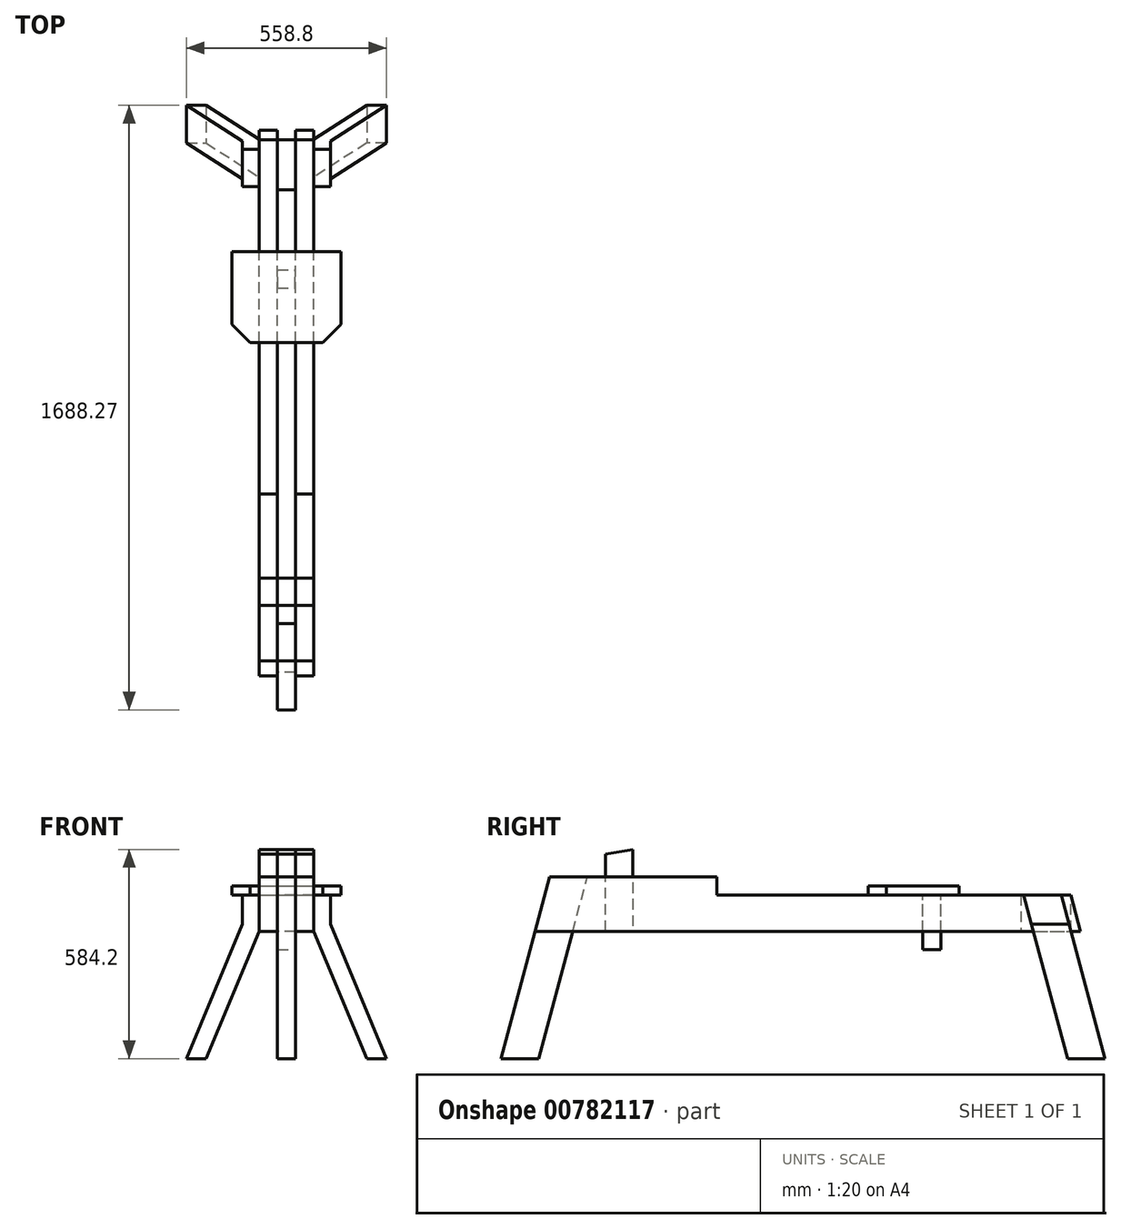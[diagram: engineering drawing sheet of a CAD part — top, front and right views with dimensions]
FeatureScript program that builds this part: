
annotation { "Feature Type Name" : "Feature", "Feature Type Description" : "" }
export const myFeature = defineFeature(function(context is Context, id is Id, definition is map)
    precondition{}
    {
        {
            var Q0;
            Q0=qCreatedBy(makeId("Right.planeOp"),FACE);
            cPlane(context, id + "F0", {"entities" : qUnion([Q0]), "cplaneType" : CPlaneType.OFFSET, "offset" : 25.4 * mm, "width" : 152.4 * mm, "height" : 152.4 * mm});
        }
        {
            var Q0;
            Q0=qCreatedBy(id+"F0.planeOp",FACE);
            var sketch = newSketch(context, id + "F1", { "sketchPlane" : qUnion([Q0])});
            skLineSegment(sketch, "E0", {"start": v(0, 0) * mm, "end": v(-40.84, -152.4) * mm});
            skLineSegment(sketch, "E1", {"start": v(0, 0) * mm, "end": v(467.16, 0) * mm});
            skLineSegment(sketch, "E2.0", {"start": v(-40.84, -152.4) * mm, "end": v(1483.16, -152.4) * mm});
            skLineSegment(sketch, "E3", {"start": v(467.16, 0) * mm, "end": v(467.16, -50.8) * mm});
            skLineSegment(sketch, "E4", {"start": v(467.16, -50.8) * mm, "end": v(1455.94, -50.8) * mm});
            skLineSegment(sketch, "E5", {"start": v(1455.94, -50.8) * mm, "end": v(1483.16, -152.4) * mm});
            skSolve(sketch);
        }
        {
            var Q0;
            Q0 = qSketchRegion(id + "F1", true);
            extrude(context, id + "F2", {"entities" : qUnion([Q0]), "depth" : 50.8 * mm, "offsetDistance" : 25.4 * mm});
        }
        {
            var Q0;
            Q0=qCreatedBy(makeId("Right.planeOp"),FACE);
            var sketch = newSketch(context, id + "F3", { "sketchPlane" : qUnion([Q0])});
            skLineSegment(sketch, "E6", {"start": v(0, 0) * mm, "end": v(-136.12, -508) * mm});
            skLineSegment(sketch, "E7", {"start": v(-136.12, -508) * mm, "end": v(-30.93, -508) * mm});
            skLineSegment(sketch, "E8", {"start": v(-30.93, -508) * mm, "end": v(105.18, 0) * mm});
            skLineSegment(sketch, "E9", {"start": v(105.18, 0) * mm, "end": v(0, 0) * mm});
            skSolve(sketch);
        }
        {
            var Q0;
            Q0 = qSketchRegion(id + "F3", true);
            extrude(context, id + "F4", {"entities" : qUnion([Q0]), "depth" : 50.8 * mm, "offsetDistance" : 25.4 * mm, "symmetric" : true});
        }
        {
            var Q0;
            Q0=makeQuery(id+"F2.opExtrude","CAP_FACE",FACE,{"disambiguationData":[OSD([sQuery(id+"F1.wireOp",EDGE,"E0"),sQuery(id+"F1.wireOp",EDGE,"E1"),sQuery(id+"F1.wireOp",EDGE,"E2.0"),sQuery(id+"F1.wireOp",EDGE,"E3"),sQuery(id+"F1.wireOp",EDGE,"E4"),sQuery(id+"F1.wireOp",EDGE,"E5")])],"isStart":false});
            var sketch = newSketch(context, id + "F5", { "sketchPlane" : qUnion([Q0])});
            skLineSegment(sketch, "E10", {"start": v(1324.46, -50.8) * mm, "end": v(1446.97, -508) * mm});
            skLineSegment(sketch, "E11", {"start": v(1446.97, -508) * mm, "end": v(1552.15, -508) * mm});
            skLineSegment(sketch, "E12", {"start": v(1552.15, -508) * mm, "end": v(1429.64, -50.8) * mm});
            skLineSegment(sketch, "E13", {"start": v(1429.64, -50.8) * mm, "end": v(1324.46, -50.8) * mm});
            skSolve(sketch);
        }
        {
            var Q0;
            Q0 = qSketchRegion(id + "F5", true);
            extrude(context, id + "F6", {"entities" : qUnion([Q0]), "depth" : 203.2 * mm, "offsetDistance" : 25.4 * mm});
        }
        {
            var Q0;
            Q0=qCreatedBy(makeId("Front.planeOp"),FACE);
            var sketch = newSketch(context, id + "F7", { "sketchPlane" : qUnion([Q0])});
            skLineSegment(sketch, "E14", {"start": v(76.2, -152.4) * mm, "end": v(224.37, -508) * mm});
            skLineSegment(sketch, "E15", {"start": v(224.37, -508) * mm, "end": v(279.4, -508) * mm, "construction": true});
            skLineSegment(sketch, "E16", {"start": v(279.4, -508) * mm, "end": v(123.1, -132.86) * mm});
            skLineSegment(sketch, "E17", {"start": v(123.1, -132.86) * mm, "end": v(123.1, -50.8) * mm});
            skLineSegment(sketch, "E18", {"start": v(123.1, -50.8) * mm, "end": v(76.2, -50.8) * mm, "construction": true});
            skLineSegment(sketch, "E19", {"start": v(76.2, -50.8) * mm, "end": v(76.2, -152.4) * mm});
            skLineSegment(sketch, "E20", {"start": v(76.2, -152.4) * mm, "end": v(123.1, -132.86) * mm, "construction": true});
            skLineSegment(sketch, "E21", {"start": v(123.1, -50.8) * mm, "end": v(279.4, -50.8) * mm});
            skLineSegment(sketch, "E22", {"start": v(279.4, -50.8) * mm, "end": v(279.4, -508) * mm});
            skLineSegment(sketch, "E23", {"start": v(224.37, -508) * mm, "end": v(76.2, -508) * mm});
            skLineSegment(sketch, "E24", {"start": v(76.2, -508) * mm, "end": v(76.2, -152.4) * mm});
            skSolve(sketch);
        }
        {
            var Q0;
            Q0 = qSketchRegion(id + "F7", true);
            extrude(context, id + "F8", {"entities" : qUnion([Q0]), "operationType" : NewBodyOperationType.REMOVE, "endBound" : BoundingType.THROUGH_ALL, "oppositeDirection" : true, "depth" : 25.4 * mm, "offsetDistance" : 25.4 * mm});
        }
        {
            var Q0;
            Q0=makeQuery(id+"F2.opExtrude","SWEPT_BODY",BODY,{"disambiguationData":[OSD([sQuery(id+"F1.wireOp",EDGE,"E0"),sQuery(id+"F1.wireOp",EDGE,"E1"),sQuery(id+"F1.wireOp",EDGE,"E2.0"),sQuery(id+"F1.wireOp",EDGE,"E3"),sQuery(id+"F1.wireOp",EDGE,"E4"),sQuery(id+"F1.wireOp",EDGE,"E5")])]});
            var Q1;
            Q1=makeQuery(id+"F6.opExtrude","SWEPT_BODY",BODY,{"disambiguationData":[OSD([sQuery(id+"F5.wireOp",EDGE,"E10"),sQuery(id+"F5.wireOp",EDGE,"E11"),sQuery(id+"F5.wireOp",EDGE,"E12"),sQuery(id+"F5.wireOp",EDGE,"E13")])]});
            var Q2;
            Q2=qCreatedBy(makeId("Right.planeOp"),FACE);
            mirror(context, id + "F9", {"entities" : qUnion([Q0, Q1]), "mirrorPlane" : qUnion([Q2])});
        }
        {
            var Q0;
            Q0=qCreatedBy(makeId("Right.planeOp"),FACE);
            var sketch = newSketch(context, id + "F10", { "sketchPlane" : qUnion([Q0])});
            skLineSegment(sketch, "E25", {"start": v(1455.94, -152.4) * mm, "end": v(1455.94, -50.8) * mm});
            skLineSegment(sketch, "E26", {"start": v(1455.94, -50.8) * mm, "end": v(1316.24, -50.8) * mm});
            skLineSegment(sketch, "E27", {"start": v(1316.24, -50.8) * mm, "end": v(1316.24, -152.4) * mm});
            skLineSegment(sketch, "E28", {"start": v(1316.24, -152.4) * mm, "end": v(1455.94, -152.4) * mm});
            skSolve(sketch);
        }
        {
            var Q0;
            Q0 = qSketchRegion(id + "F10", true);
            extrude(context, id + "F11", {"entities" : qUnion([Q0]), "depth" : 50.8 * mm, "offsetDistance" : 25.4 * mm, "symmetric" : true});
        }
        {
            var Q0;
            Q0=makeQuery(id+"F2.opExtrude","SWEPT_FACE",FACE,{"disambiguationData":[OSD([sQuery(id+"F1.wireOp",EDGE,"E4")])]});
            var sketch = newSketch(context, id + "F12", { "sketchPlane" : qUnion([Q0])});
            skLineSegment(sketch, "E29", {"start": v(0, 1143.85) * mm, "end": v(152.4, 1143.85) * mm});
            skLineSegment(sketch, "E30", {"start": v(152.4, 1143.85) * mm, "end": v(152.4, 940.65) * mm});
            skLineSegment(sketch, "E31", {"start": v(101.6, 889.85) * mm, "end": v(152.4, 940.65) * mm});
            skLineSegment(sketch, "E32", {"start": v(101.6, 889.85) * mm, "end": v(0, 889.85) * mm});
            skLineSegment(sketch, "E33", {"start": v(0, 1143.85) * mm, "end": v(0, 889.85) * mm, "construction": true});
            skLineSegment(sketch, "E34.MirrorCS", {"start": v(0, 1143.85) * mm, "end": v(-152.4, 1143.85) * mm});
            skLineSegment(sketch, "E35.MirrorCS", {"start": v(-152.4, 1143.85) * mm, "end": v(-152.4, 940.65) * mm});
            skLineSegment(sketch, "E36.MirrorCS", {"start": v(-101.6, 889.85) * mm, "end": v(-152.4, 940.65) * mm});
            skLineSegment(sketch, "E37.MirrorCS", {"start": v(-101.6, 889.85) * mm, "end": v(0, 889.85) * mm});
            skSolve(sketch);
        }
        {
            var Q0;
            Q0 = qSketchRegion(id + "F12", true);
            extrude(context, id + "F13", {"entities" : qUnion([Q0]), "depth" : 25.4 * mm, "offsetDistance" : 25.4 * mm});
        }
        {
            var Q0;
            Q0=makeQuery(id+"F13.opExtrude","CAP_FACE",FACE,{"disambiguationData":[OSD([sQuery(id+"F12.wireOp",EDGE,"E29"),sQuery(id+"F12.wireOp",EDGE,"E30"),sQuery(id+"F12.wireOp",EDGE,"E31"),sQuery(id+"F12.wireOp",EDGE,"E32"),sQuery(id+"F12.wireOp",EDGE,"E34.MirrorCS"),sQuery(id+"F12.wireOp",EDGE,"E35.MirrorCS"),sQuery(id+"F12.wireOp",EDGE,"E36.MirrorCS"),sQuery(id+"F12.wireOp",EDGE,"E37.MirrorCS")])],"isStart":true});
            var sketch = newSketch(context, id + "F14", { "sketchPlane" : qUnion([Q0])});
            skLineSegment(sketch, "E38.bottom", {"start": v(-24.6, -1042.25) * mm, "end": v(24.6, -1042.25) * mm});
            skLineSegment(sketch, "E38.top", {"start": v(-24.6, -1093.05) * mm, "end": v(24.6, -1093.05) * mm});
            skLineSegment(sketch, "E38.left", {"start": v(-24.6, -1042.25) * mm, "end": v(-24.6, -1093.05) * mm});
            skLineSegment(sketch, "E38.right", {"start": v(24.6, -1042.25) * mm, "end": v(24.6, -1093.05) * mm});
            skSolve(sketch);
        }
        {
            var Q0;
            Q0 = qSketchRegion(id + "F14", true);
            extrude(context, id + "F15", {"entities" : qUnion([Q0]), "depth" : 152.4 * mm, "offsetDistance" : 25.4 * mm});
        }
        {
            var Q0;
            Q0=qCreatedBy(makeId("Right.planeOp"),FACE);
            var sketch = newSketch(context, id + "F16", { "sketchPlane" : qUnion([Q0])});
            skLineSegment(sketch, "E39", {"start": v(155.98, -152.4) * mm, "end": v(155.98, 62.76) * mm});
            skLineSegment(sketch, "E40", {"start": v(232.18, 76.2) * mm, "end": v(232.18, -152.4) * mm});
            skLineSegment(sketch, "E41", {"start": v(155.98, -152.4) * mm, "end": v(232.18, -152.4) * mm});
            skLineSegment(sketch, "E42", {"start": v(232.18, 76.2) * mm, "end": v(155.98, 62.76) * mm});
            skSolve(sketch);
        }
        {
            var Q0;
            Q0 = qSketchRegion(id + "F16", true);
            extrude(context, id + "F17", {"entities" : qUnion([Q0]), "depth" : 50.8 * mm, "offsetDistance" : 25.4 * mm, "symmetric" : true});
        }
        {
            var Q0;
            Q0=makeQuery(id+"F17.opExtrude","CAP_FACE",FACE,{"disambiguationData":[OSD([sQuery(id+"F16.wireOp",EDGE,"E39"),sQuery(id+"F16.wireOp",EDGE,"xzLFHn83-Cl1C-1Pvl-YwiQ-3eKPHtVyysRk"),sQuery(id+"F16.wireOp",EDGE,"E40"),sQuery(id+"F16.wireOp",EDGE,"E41")])],"isStart":false});
            var sketch = newSketch(context, id + "F18", { "sketchPlane" : qUnion([Q0])});
            skLineSegment(sketch, "E43.0", {"start": v(232.18, 76.2) * mm, "end": v(155.98, 62.76) * mm});
            skLineSegment(sketch, "E44.0", {"start": v(155.98, 0) * mm, "end": v(155.98, 62.76) * mm});
            skLineSegment(sketch, "E45.0", {"start": v(232.18, 76.2) * mm, "end": v(232.18, 0) * mm});
            skLineSegment(sketch, "E46.0", {"start": v(155.98, 0) * mm, "end": v(232.18, 0) * mm});
            skPoint(sketch, "E47.orphan", {"position": v(0, 0) * mm});
            skPoint(sketch, "E48.orphan", {"position": v(155.98, -152.4) * mm});
            skPoint(sketch, "E49.orphan", {"position": v(232.18, -152.4) * mm});
            skPoint(sketch, "E50.orphan", {"position": v(467.16, 0) * mm});
            skSolve(sketch);
        }
        {
            var Q0;
            Q0 = qSketchRegion(id + "F18", true);
            extrude(context, id + "F19", {"entities" : qUnion([Q0]), "depth" : 50.8 * mm, "offsetDistance" : 25.4 * mm});
        }
        {
            var Q0;
            Q0=makeQuery(id+"F19.opExtrude","SWEPT_BODY",BODY,{"disambiguationData":[OSD([sQuery(id+"F18.wireOp",EDGE,"E43.0"),sQuery(id+"F18.wireOp",EDGE,"E44.0"),sQuery(id+"F18.wireOp",EDGE,"E45.0"),sQuery(id+"F18.wireOp",EDGE,"E46.0")])]});
            var Q1;
            Q1=qCreatedBy(makeId("Right.planeOp"),FACE);
            mirror(context, id + "F20", {"entities" : qUnion([Q0]), "mirrorPlane" : qUnion([Q1])});
        }
    });
